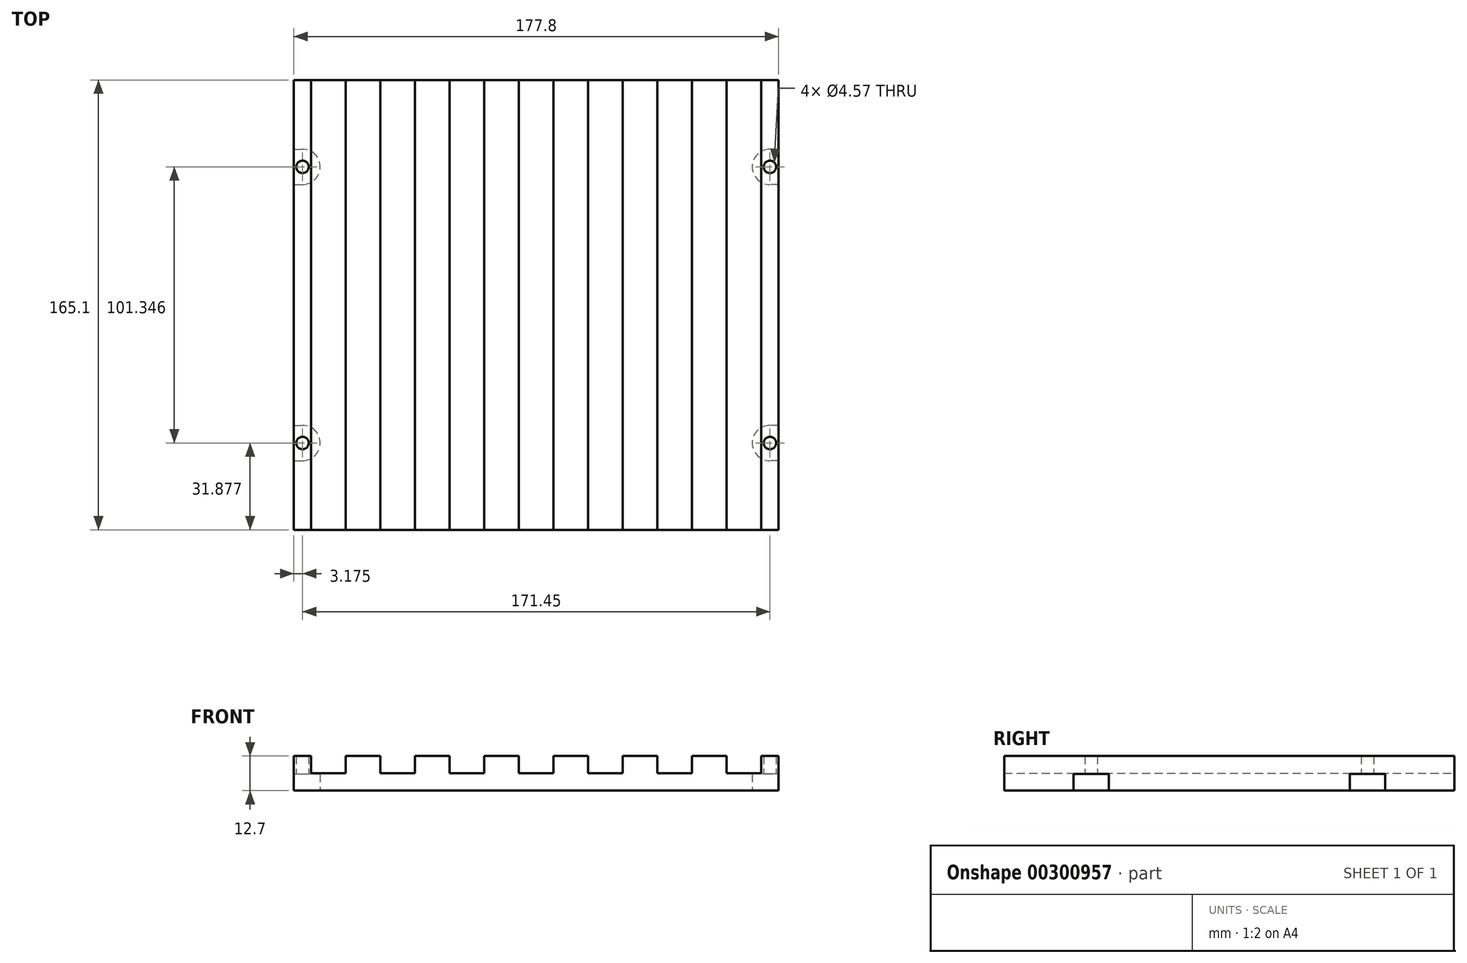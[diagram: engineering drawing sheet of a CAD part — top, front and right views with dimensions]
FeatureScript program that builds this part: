
annotation { "Feature Type Name" : "Feature", "Feature Type Description" : "" }
export const myFeature = defineFeature(function(context is Context, id is Id, definition is map)
    precondition{}
    {
        {
            var Q0;
            Q0=qCreatedBy(makeId("Front.planeOp"),FACE);
            var sketch = newSketch(context, id + "F0", { "sketchPlane" : qUnion([Q0])});
            skLineSegment(sketch, "E0.bottom", {"start": v(-88.9, 0) * mm, "end": v(88.9, 0) * mm});
            skLineSegment(sketch, "E0.top", {"start": v(-88.9, 12.7) * mm, "end": v(-82.55, 12.7) * mm});
            skLineSegment(sketch, "E0.left", {"start": v(-88.9, 0) * mm, "end": v(-88.9, 12.7) * mm});
            skLineSegment(sketch, "E0.right", {"start": v(88.9, 0) * mm, "end": v(88.9, 12.7) * mm});
            skLineSegment(sketch, "E1", {"start": v(-82.55, 12.7) * mm, "end": v(-82.55, 6.35) * mm});
            skLineSegment(sketch, "E2", {"start": v(-82.55, 6.35) * mm, "end": v(-69.85, 6.35) * mm});
            skLineSegment(sketch, "E3", {"start": v(-69.85, 6.35) * mm, "end": v(-69.85, 12.7) * mm});
            skLineSegment(sketch, "E4.trimOffspring", {"start": v(-69.85, 12.7) * mm, "end": v(-57.15, 12.7) * mm});
            skLineSegment(sketch, "E5.1.0.0", {"start": v(-57.15, 12.7) * mm, "end": v(-57.15, 6.35) * mm});
            skLineSegment(sketch, "E5.1.0.1", {"start": v(-57.15, 6.35) * mm, "end": v(-44.45, 6.35) * mm});
            skLineSegment(sketch, "E5.1.0.2", {"start": v(-44.45, 6.35) * mm, "end": v(-44.45, 12.7) * mm});
            skLineSegment(sketch, "E5.2.0.0", {"start": v(-31.75, 12.7) * mm, "end": v(-31.75, 6.35) * mm});
            skLineSegment(sketch, "E5.2.0.1", {"start": v(-31.75, 6.35) * mm, "end": v(-19.05, 6.35) * mm});
            skLineSegment(sketch, "E5.2.0.2", {"start": v(-19.05, 6.35) * mm, "end": v(-19.05, 12.7) * mm});
            skLineSegment(sketch, "E5.3.0.0", {"start": v(-6.35, 12.7) * mm, "end": v(-6.35, 6.35) * mm});
            skLineSegment(sketch, "E5.3.0.1", {"start": v(-6.35, 6.35) * mm, "end": v(6.35, 6.35) * mm});
            skLineSegment(sketch, "E5.3.0.2", {"start": v(6.35, 6.35) * mm, "end": v(6.35, 12.7) * mm});
            skLineSegment(sketch, "E5.4.0.0", {"start": v(19.05, 12.7) * mm, "end": v(19.05, 6.35) * mm});
            skLineSegment(sketch, "E5.4.0.1", {"start": v(19.05, 6.35) * mm, "end": v(31.75, 6.35) * mm});
            skLineSegment(sketch, "E5.4.0.2", {"start": v(31.75, 6.35) * mm, "end": v(31.75, 12.7) * mm});
            skLineSegment(sketch, "E5.5.0.0", {"start": v(44.45, 12.7) * mm, "end": v(44.45, 6.35) * mm});
            skLineSegment(sketch, "E5.5.0.1", {"start": v(44.45, 6.35) * mm, "end": v(57.15, 6.35) * mm});
            skLineSegment(sketch, "E5.5.0.2", {"start": v(57.15, 6.35) * mm, "end": v(57.15, 12.7) * mm});
            skLineSegment(sketch, "E5.6.0.0", {"start": v(69.85, 12.7) * mm, "end": v(69.85, 6.35) * mm});
            skLineSegment(sketch, "E5.6.0.1", {"start": v(69.85, 6.35) * mm, "end": v(82.55, 6.35) * mm});
            skLineSegment(sketch, "E5.6.0.2", {"start": v(82.55, 6.35) * mm, "end": v(82.55, 12.7) * mm});
            skLineSegment(sketch, "E5.direction1", {"start": v(-82.55, 6.35) * mm, "end": v(-57.15, 6.35) * mm, "construction": true});
            skLineSegment(sketch, "E6.trimOffspring", {"start": v(-44.45, 12.7) * mm, "end": v(-31.75, 12.7) * mm});
            skLineSegment(sketch, "E7.trimOffspring", {"start": v(-19.05, 12.7) * mm, "end": v(-6.35, 12.7) * mm});
            skLineSegment(sketch, "E8.trimOffspring", {"start": v(6.35, 12.7) * mm, "end": v(19.05, 12.7) * mm});
            skLineSegment(sketch, "E9.trimOffspring", {"start": v(31.75, 12.7) * mm, "end": v(44.45, 12.7) * mm});
            skLineSegment(sketch, "E10.trimOffspring", {"start": v(57.15, 12.7) * mm, "end": v(69.85, 12.7) * mm});
            skLineSegment(sketch, "E11.trimOffspring", {"start": v(82.55, 12.7) * mm, "end": v(88.9, 12.7) * mm});
            skLineSegment(sketch, "E12", {"start": v(88.9, 12.7) * mm, "end": v(88.9, 6.35) * mm});
            skSolve(sketch);
        }
        {
            var Q0;
            Q0=qSketchRegion(id+"F0",true);
            extrude(context, id + "F1", {"entities" : qUnion([Q0]), "depth" : 165.1 * mm});
        }
        {
            var Q0;
            Q0=makeQuery(id+"F1.opExtrude","SWEPT_FACE",FACE,{"disambiguationData":[OSD([sQuery(id+"F0.wireOp",EDGE,"E0.bottom")])]});
            var sketch = newSketch(context, id + "F2", { "sketchPlane" : qUnion([Q0])});
            skLineSegment(sketch, "E13.bottom", {"start": v(88.9, 126.75) * mm, "end": v(85.72, 126.75) * mm});
            skLineSegment(sketch, "E13.top", {"start": v(88.9, 139.7) * mm, "end": v(85.72, 139.7) * mm});
            skLineSegment(sketch, "E13.left", {"start": v(88.9, 126.75) * mm, "end": v(88.9, 139.7) * mm});
            skArc(sketch, "E14", {"start": v(85.72, 139.7) * mm, "mid": v(79.25, 133.22) * mm, "end": v(85.72, 126.75) * mm});
            skLineSegment(sketch, "E15", {"start": v(-88.9, 82.55) * mm, "end": v(88.9, 82.55) * mm, "construction": true});
            skLineSegment(sketch, "E16", {"start": v(0, 165.1) * mm, "end": v(0, 0) * mm, "construction": true});
            skLineSegment(sketch, "E17.MirrorCS", {"start": v(88.9, 38.35) * mm, "end": v(88.9, 25.4) * mm});
            skLineSegment(sketch, "E18.MirrorCS", {"start": v(88.9, 38.35) * mm, "end": v(85.72, 38.35) * mm});
            skArc(sketch, "E19.MirrorCS", {"start": v(85.72, 25.4) * mm, "mid": v(79.25, 31.88) * mm, "end": v(85.72, 38.35) * mm});
            skLineSegment(sketch, "E20.MirrorCS", {"start": v(88.9, 25.4) * mm, "end": v(85.72, 25.4) * mm});
            skLineSegment(sketch, "E21.MirrorCS", {"start": v(-88.9, 126.75) * mm, "end": v(-88.9, 139.7) * mm});
            skLineSegment(sketch, "E22.MirrorCS", {"start": v(-88.9, 38.35) * mm, "end": v(-88.9, 25.4) * mm});
            skLineSegment(sketch, "E23.MirrorCS", {"start": v(-88.9, 38.35) * mm, "end": v(-85.72, 38.35) * mm});
            skLineSegment(sketch, "E24.MirrorCS", {"start": v(-88.9, 139.7) * mm, "end": v(-85.72, 139.7) * mm});
            skLineSegment(sketch, "E25.MirrorCS", {"start": v(-88.9, 25.4) * mm, "end": v(-85.72, 25.4) * mm});
            skLineSegment(sketch, "E26.MirrorCS", {"start": v(-88.9, 126.75) * mm, "end": v(-85.72, 126.75) * mm});
            skLineSegment(sketch, "E27.MirrorCS", {"start": v(88.9, 82.55) * mm, "end": v(-88.9, 82.55) * mm, "construction": true});
            skArc(sketch, "E28.MirrorCS", {"start": v(-85.72, 25.4) * mm, "mid": v(-79.25, 31.88) * mm, "end": v(-85.72, 38.35) * mm});
            skArc(sketch, "E29.MirrorCS", {"start": v(-85.72, 139.7) * mm, "mid": v(-79.25, 133.22) * mm, "end": v(-85.72, 126.75) * mm});
            skSolve(sketch);
        }
        {
            var Q0;
            Q0 = qSketchRegion(id + "F2", true);
            extrude(context, id + "F3", {"entities" : qUnion([Q0]), "operationType" : NewBodyOperationType.REMOVE, "oppositeDirection" : true, "depth" : 6.1 * mm});
        }
        {
            var Q0;
            Q0=makeQuery(id+"F1.opExtrude","SWEPT_FACE",FACE,{"disambiguationData":[OSD([sQuery(id+"F0.wireOp",EDGE,"E0.bottom")])]});
            var sketch = newSketch(context, id + "F4", { "sketchPlane" : qUnion([Q0])});
            skCircle(sketch, "E30", {"center": v(-85.72, 133.22) * mm, "radius": 2.29 * mm});
            skCircle(sketch, "E31.MirrorC", {"center": v(85.72, 133.22) * mm, "radius": 2.29 * mm});
            skCircle(sketch, "E32.MirrorC", {"center": v(85.72, 31.88) * mm, "radius": 2.29 * mm});
            skCircle(sketch, "E33.MirrorC", {"center": v(-85.72, 31.88) * mm, "radius": 2.29 * mm});
            skSolve(sketch);
        }
        {
            var Q0;
            Q0 = qSketchRegion(id + "F4", true);
            extrude(context, id + "F5", {"entities" : qUnion([Q0]), "operationType" : NewBodyOperationType.REMOVE, "oppositeDirection" : true, "depth" : 25.4 * mm});
        }
        {
            var Q0;
            Q0=qCreatedBy(makeId("Right.planeOp"),FACE);
            cPlane(context, id + "F6", {"entities" : qUnion([Q0]), "cplaneType" : CPlaneType.OFFSET, "offset" : 76.2 * mm, "width" : 152.4 * mm, "height" : 152.4 * mm});
        }
    });
